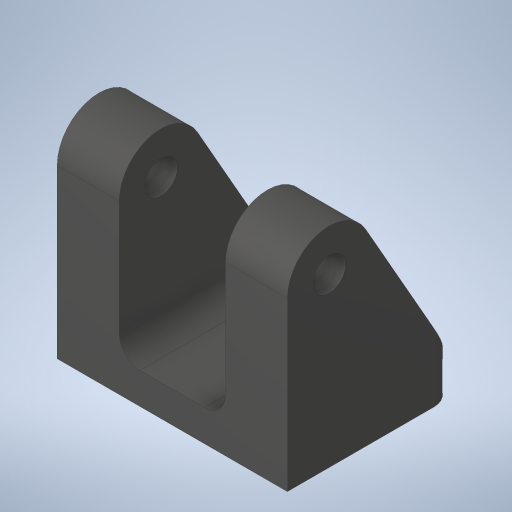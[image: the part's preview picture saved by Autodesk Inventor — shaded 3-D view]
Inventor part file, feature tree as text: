
AUTODESK INVENTOR PART (.ipt)
format: ipt  version: 2023.4 (Build 274418000, 418)  size: 242,176 bytes
history: native  units: in
note: dims shown in document units (in); Inventor stores cm internally (conversion verified against a paired STEP export)
features: fillet x1
ambient origin geometry x8: Origin, YZ Plane, XZ Plane, XY Plane, X Axis, Y Axis, Z Axis, Center Point
bodies: Solid1 (feature_tree)
feature tree (1):
  fillet  "Fillet2"  [1 undecoded]
note: 1 required parameter value undecoded (feature->parameter linkage not recoverable at this tier; creation-order binding heuristic only, values carry confidence <= 0.55)
